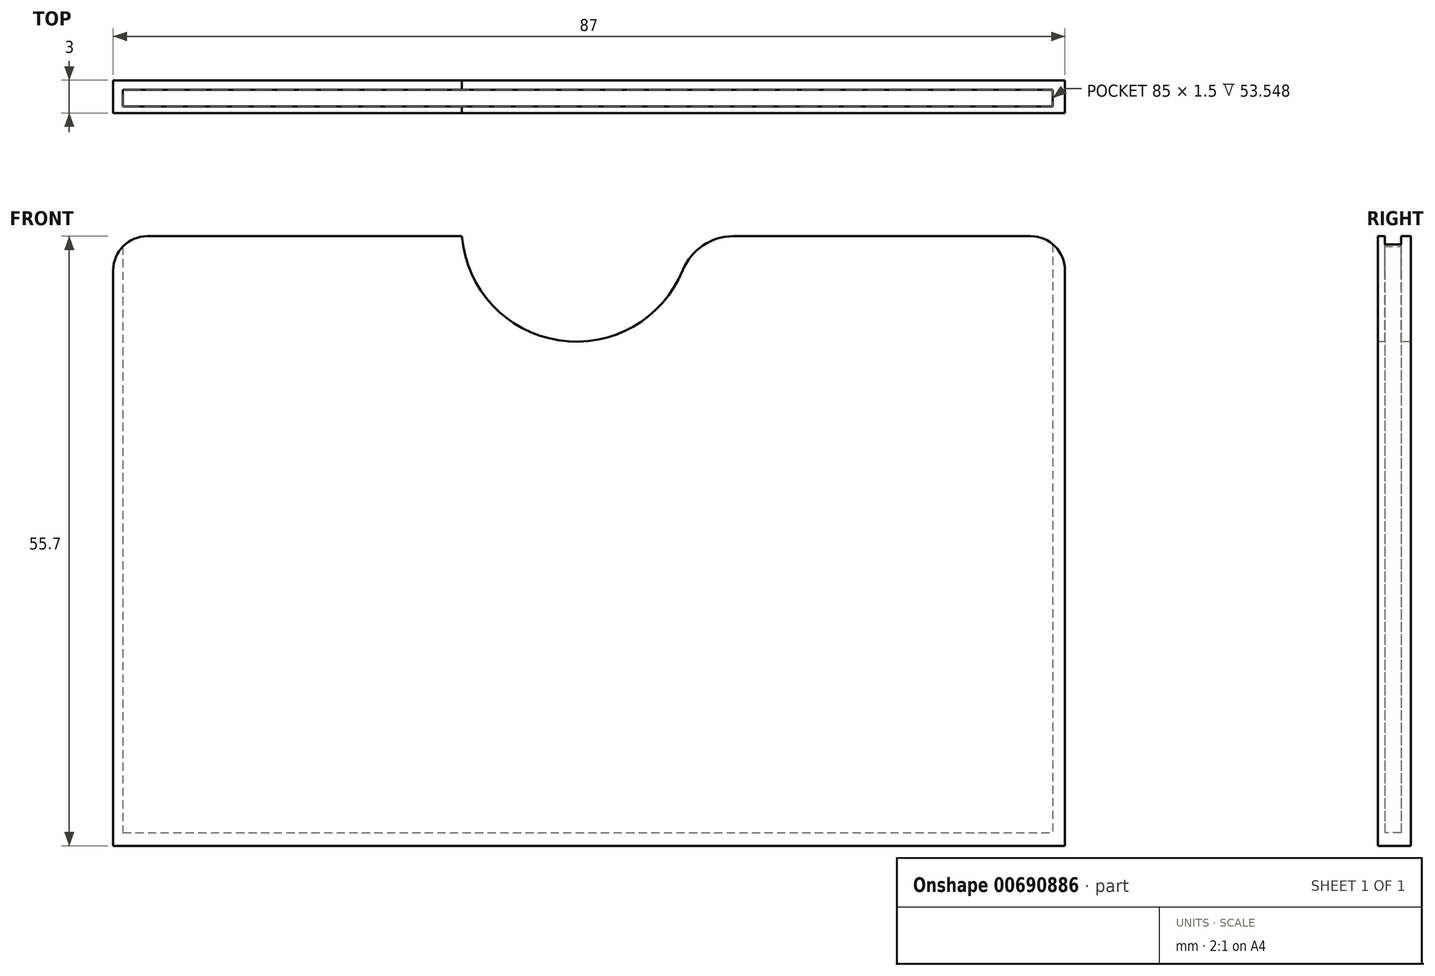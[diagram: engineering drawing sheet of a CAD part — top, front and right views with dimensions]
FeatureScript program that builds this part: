
annotation { "Feature Type Name" : "Feature", "Feature Type Description" : "" }
export const myFeature = defineFeature(function(context is Context, id is Id, definition is map)
    precondition{}
    {
        {
            var Q0;
            Q0=qCreatedBy(makeId("Top.planeOp"),FACE);
            var sketch = newSketch(context, id + "F0", { "sketchPlane" : qUnion([Q0])});
            skLineSegment(sketch, "E0.bottom", {"start": v(-24.68, 16.15) * mm, "end": v(62.32, 16.15) * mm});
            skLineSegment(sketch, "E0.top", {"start": v(-24.68, 13.15) * mm, "end": v(62.32, 13.15) * mm});
            skLineSegment(sketch, "E0.left", {"start": v(-24.68, 16.15) * mm, "end": v(-24.68, 13.15) * mm});
            skLineSegment(sketch, "E0.right", {"start": v(62.32, 16.15) * mm, "end": v(62.32, 13.15) * mm});
            skLineSegment(sketch, "E1.bottom", {"start": v(-23.8, 15.26) * mm, "end": v(61.2, 15.26) * mm});
            skLineSegment(sketch, "E1.top", {"start": v(-23.8, 13.76) * mm, "end": v(61.2, 13.76) * mm});
            skLineSegment(sketch, "E1.left", {"start": v(-23.8, 15.26) * mm, "end": v(-23.8, 13.76) * mm});
            skLineSegment(sketch, "E1.right", {"start": v(61.2, 15.26) * mm, "end": v(61.2, 13.76) * mm});
            skSolve(sketch);
        }
        {
            var Q0;
            Q0=makeQuery(id+"F0.imprint","IMPRINT",FACE,{"disambiguationData":[TD([[makeQuery(id+"F0.imprint","IMPRINT",EDGE,{"derivedFrom":sQuery(id+"F0.wireOp",EDGE,"E0.bottom")}),-1.0]])]});
            extrude(context, id + "F1", {"entities" : qUnion([Q0]), "depth" : 54.5 * mm, "offsetDistance" : 25 * mm});
        }
        {
            var Q0;
            Q0=makeQuery(id+"F1.opExtrude","SWEPT_FACE",FACE,{"disambiguationData":[OSD([sQuery(id+"F0.wireOp",EDGE,"E0.top")])]});
            var sketch = newSketch(context, id + "F2", { "sketchPlane" : qUnion([Q0])});
            skCircle(sketch, "E2", {"center": v(17.66, 55.36) * mm, "radius": 10.5 * mm});
            skPoint(sketch, "E2.first.point", {"position": v(7.2, 54.5) * mm});
            skPoint(sketch, "E2.second.point", {"position": v(28.13, 54.5) * mm});
            skPoint(sketch, "E2.third.point", {"position": v(17.53, 44.86) * mm});
            skSolve(sketch);
        }
        {
            var Q0;
            {var subQ0=sQuery(id+"F2.wireOp",EDGE,"E2");var subQ1=makeQuery(id+"F1.opExtrude","CAP_EDGE",EDGE,{"disambiguationData":[OSD([sQuery(id+"F0.wireOp",EDGE,"E0.top")])],"isStart":false});var subQ2=makeQuery(id+"F2.imprint","INTERSECT",VERTEX,{"disambiguationData":[OD(0.0)],"derivedFrom":[subQ1,subQ0]});Q0=makeQuery(id+"F2.imprint","IMPRINT",FACE,{"disambiguationData":[TD([[makeQuery(id+"F2.imprint","IMPRINT",EDGE,{"disambiguationData":[TD([[subQ2,-1.0]])],"derivedFrom":subQ0}),1.0]])]});}
            extrude(context, id + "F3", {"entities" : qUnion([Q0]), "operationType" : NewBodyOperationType.REMOVE, "depth" : -10 * mm, "offsetDistance" : 25 * mm});
        }
        {
            var Q0;
            Q0=makeQuery(id+"F1.opExtrude","CAP_EDGE",EDGE,{"disambiguationData":[OSD([sQuery(id+"F0.wireOp",EDGE,"E0.right")])],"isStart":false});
            fillet(context, id + "F4", {"entities" : qUnion([Q0]), "radius" : 3.14 * mm, "tangentPropagation" : true, "allowEdgeOverflow" : false});
        }
        {
            var Q0;
            Q0=makeQuery(id+"F1.opExtrude","CAP_EDGE",EDGE,{"disambiguationData":[OSD([sQuery(id+"F0.wireOp",EDGE,"E0.left")])],"isStart":false});
            fillet(context, id + "F5", {"entities" : qUnion([Q0]), "radius" : 3.14 * mm, "tangentPropagation" : true, "allowEdgeOverflow" : false});
        }
        {
            var Q0;
            Q0=qCreatedBy(makeId("Top.planeOp"),FACE);
            var sketch = newSketch(context, id + "F6", { "sketchPlane" : qUnion([Q0])});
            skPoint(sketch, "E3.0", {"position": v(-23.8, 13.76) * mm});
            skLineSegment(sketch, "E4.0", {"start": v(-24.68, 13.15) * mm, "end": v(62.32, 13.15) * mm});
            skLineSegment(sketch, "E5.0", {"start": v(-24.68, 16.15) * mm, "end": v(62.32, 16.15) * mm});
            skLineSegment(sketch, "E6.0", {"start": v(62.32, 16.15) * mm, "end": v(62.32, 13.15) * mm});
            skLineSegment(sketch, "E7.0", {"start": v(-24.68, 16.15) * mm, "end": v(-24.68, 13.15) * mm});
            skSolve(sketch);
        }
        {
            var Q0;
            Q0 = qSketchRegion(id + "F6", true);
            extrude(context, id + "F7", {"entities" : qUnion([Q0]), "operationType" : NewBodyOperationType.ADD, "oppositeDirection" : true, "depth" : 1.2 * mm, "offsetDistance" : 25 * mm});
        }
        {
            var Q0;
            {var subQ1=sQuery(id+"F0.wireOp",EDGE,"E0.top");var subQ2=sQuery(id+"F2.wireOp",EDGE,"E2");Q0=makeQuery(id+"F3.boolean.opBoolean","COPY",EDGE,{"disambiguationData":[TD([makeQuery(id+"F1.opExtrude","SWEPT_FACE",FACE,{"disambiguationData":[OSD([subQ1])]})])],"derivedFrom":makeQuery(id+"F3.opExtrude","SWEPT_EDGE",EDGE,{"disambiguationData":[OSD([subQ1,subQ2]),TDD([makeQuery(id+"F2.imprint","INTERSECT",VERTEX,{"disambiguationData":[OD(1.0)],"derivedFrom":[makeQuery(id+"F1.opExtrude","CAP_EDGE",EDGE,{"disambiguationData":[OSD([subQ1])],"isStart":false}),subQ2]})])]})});}
            var Q1;
            {var subQ0=sQuery(id+"F0.wireOp",EDGE,"E0.bottom");var subQ2=sQuery(id+"F0.wireOp",EDGE,"E0.top");var subQ3=sQuery(id+"F2.wireOp",EDGE,"E2");Q1=makeQuery(id+"F3.boolean.opBoolean","COPY",EDGE,{"disambiguationData":[TD([makeQuery(id+"F1.opExtrude","SWEPT_FACE",FACE,{"disambiguationData":[OSD([subQ0])]})])],"derivedFrom":makeQuery(id+"F3.opExtrude","SWEPT_EDGE",EDGE,{"disambiguationData":[OSD([subQ2,subQ3]),TDD([makeQuery(id+"F2.imprint","INTERSECT",VERTEX,{"disambiguationData":[OD(1.0)],"derivedFrom":[makeQuery(id+"F1.opExtrude","CAP_EDGE",EDGE,{"disambiguationData":[OSD([subQ2])],"isStart":false}),subQ3]})])]})});}
            var Q2;
            {var subQ1=sQuery(id+"F0.wireOp",EDGE,"E0.top");var subQ2=sQuery(id+"F2.wireOp",EDGE,"E2");Q2=makeQuery(id+"F3.boolean.opBoolean","COPY",EDGE,{"disambiguationData":[TD([makeQuery(id+"F1.opExtrude","SWEPT_FACE",FACE,{"disambiguationData":[OSD([subQ1])]})])],"derivedFrom":makeQuery(id+"F3.opExtrude","SWEPT_EDGE",EDGE,{"disambiguationData":[OSD([subQ1,subQ2]),TDD([makeQuery(id+"F2.imprint","INTERSECT",VERTEX,{"disambiguationData":[OD(0.0)],"derivedFrom":[makeQuery(id+"F1.opExtrude","CAP_EDGE",EDGE,{"disambiguationData":[OSD([subQ1])],"isStart":false}),subQ2]})])]})});}
            var Q3;
            {var subQ0=sQuery(id+"F0.wireOp",EDGE,"E0.bottom");var subQ2=sQuery(id+"F0.wireOp",EDGE,"E0.top");var subQ3=sQuery(id+"F2.wireOp",EDGE,"E2");Q3=makeQuery(id+"F3.boolean.opBoolean","COPY",EDGE,{"disambiguationData":[TD([makeQuery(id+"F1.opExtrude","SWEPT_FACE",FACE,{"disambiguationData":[OSD([subQ0])]})])],"derivedFrom":makeQuery(id+"F3.opExtrude","SWEPT_EDGE",EDGE,{"disambiguationData":[OSD([subQ2,subQ3]),TDD([makeQuery(id+"F2.imprint","INTERSECT",VERTEX,{"disambiguationData":[OD(0.0)],"derivedFrom":[makeQuery(id+"F1.opExtrude","CAP_EDGE",EDGE,{"disambiguationData":[OSD([subQ2])],"isStart":false}),subQ3]})])]})});}
            fillet(context, id + "F8", {"entities" : qUnion([Q0, Q1, Q2, Q3]), "radius" : 5 * mm, "tangentPropagation" : true, "allowEdgeOverflow" : false});
        }
    });
